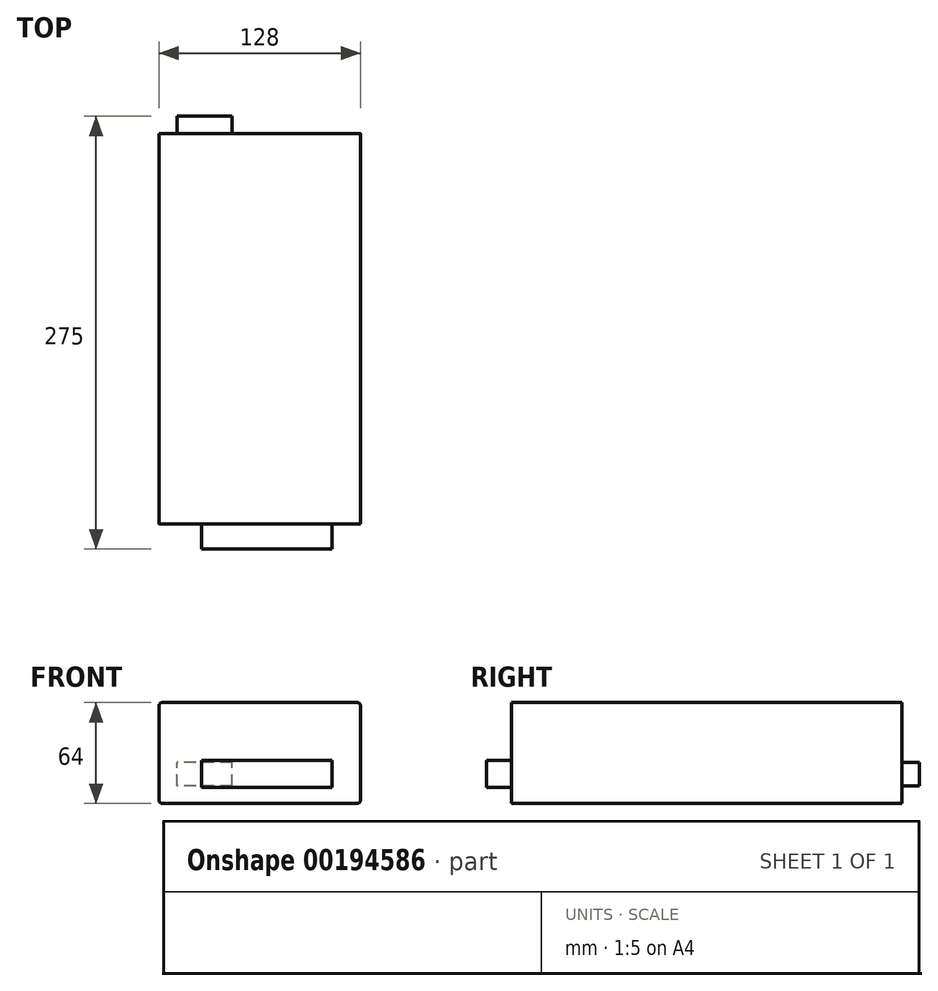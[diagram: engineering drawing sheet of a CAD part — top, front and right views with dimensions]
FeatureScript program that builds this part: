
annotation { "Feature Type Name" : "Feature", "Feature Type Description" : "" }
export const myFeature = defineFeature(function(context is Context, id is Id, definition is map)
    precondition{}
    {
        {
            var Q0;
            Q0=qCreatedBy(makeId("Front.planeOp"),FACE);
            var sketch = newSketch(context, id + "F0", { "sketchPlane" : qUnion([Q0])});
            skLineSegment(sketch, "E0.bottom", {"start": v(0, 0) * mm, "end": v(128, 0) * mm});
            skLineSegment(sketch, "E0.top", {"start": v(0, 64) * mm, "end": v(128, 64) * mm});
            skLineSegment(sketch, "E0.left", {"start": v(0, 0) * mm, "end": v(0, 64) * mm});
            skLineSegment(sketch, "E0.right", {"start": v(128, 0) * mm, "end": v(128, 64) * mm});
            skSolve(sketch);
        }
        {
            var Q0;
            Q0 = qSketchRegion(id + "F0", true);
            extrude(context, id + "F1", {"entities" : qUnion([Q0]), "depth" : 248 * mm});
        }
        {
            var Q0;
            Q0=makeQuery(id+"F1.opExtrude","CAP_FACE",FACE,{"disambiguationData":[OSD([sQuery(id+"F0.wireOp",EDGE,"E0.bottom"),sQuery(id+"F0.wireOp",EDGE,"E0.top"),sQuery(id+"F0.wireOp",EDGE,"E0.left"),sQuery(id+"F0.wireOp",EDGE,"E0.right")])],"isStart":false});
            var sketch = newSketch(context, id + "F2", { "sketchPlane" : qUnion([Q0])});
            skLineSegment(sketch, "E1", {"start": v(110, 10) * mm, "end": v(27, 10) * mm});
            skLineSegment(sketch, "E2", {"start": v(27, 10) * mm, "end": v(27, 27.33) * mm});
            skLineSegment(sketch, "E3", {"start": v(27, 27.33) * mm, "end": v(110, 27.33) * mm});
            skLineSegment(sketch, "E4", {"start": v(110, 27.33) * mm, "end": v(110, 10) * mm});
            skSolve(sketch);
        }
        {
            var Q0;
            Q0 = qSketchRegion(id + "F2", true);
            extrude(context, id + "F3", {"entities" : qUnion([Q0]), "operationType" : NewBodyOperationType.ADD, "depth" : 16 * mm});
        }
        {
            var Q0;
            Q0=makeQuery(id+"F1.opExtrude","CAP_FACE",FACE,{"disambiguationData":[OSD([sQuery(id+"F0.wireOp",EDGE,"E0.bottom"),sQuery(id+"F0.wireOp",EDGE,"E0.top"),sQuery(id+"F0.wireOp",EDGE,"E0.left"),sQuery(id+"F0.wireOp",EDGE,"E0.right")])],"isStart":true});
            var sketch = newSketch(context, id + "F4", { "sketchPlane" : qUnion([Q0])});
            skLineSegment(sketch, "E5.bottom", {"start": v(-46.5, 11) * mm, "end": v(-11.5, 11) * mm});
            skLineSegment(sketch, "E5.top", {"start": v(-46.5, 26) * mm, "end": v(-11.5, 26) * mm});
            skLineSegment(sketch, "E5.left", {"start": v(-46.5, 11) * mm, "end": v(-46.5, 26) * mm});
            skLineSegment(sketch, "E5.right", {"start": v(-11.5, 11) * mm, "end": v(-11.5, 26) * mm});
            skSolve(sketch);
        }
        {
            var Q0;
            Q0 = qSketchRegion(id + "F4", true);
            extrude(context, id + "F5", {"entities" : qUnion([Q0]), "operationType" : NewBodyOperationType.ADD, "depth" : 11 * mm});
        }
        {
            var Q0;
            Q0=makeQuery(id+"F1.opExtrude","SWEPT_EDGE",EDGE,{"disambiguationData":[OSD([sQuery(id+"F0.wireOp",EDGE,"E0.top"),sQuery(id+"F0.wireOp",EDGE,"E0.right")])]});
            var Q1;
            Q1=makeQuery(id+"F1.opExtrude","SWEPT_EDGE",EDGE,{"disambiguationData":[OSD([sQuery(id+"F0.wireOp",EDGE,"E0.bottom"),sQuery(id+"F0.wireOp",EDGE,"E0.right")])]});
            var Q2;
            Q2=makeQuery(id+"F1.opExtrude","SWEPT_EDGE",EDGE,{"disambiguationData":[OSD([sQuery(id+"F0.wireOp",EDGE,"E0.top"),sQuery(id+"F0.wireOp",EDGE,"E0.left")])]});
            var Q3;
            Q3=makeQuery(id+"F1.opExtrude","SWEPT_EDGE",EDGE,{"disambiguationData":[OSD([sQuery(id+"F0.wireOp",EDGE,"E0.bottom"),sQuery(id+"F0.wireOp",EDGE,"E0.left")])]});
            fillet(context, id + "F6", {"entities" : qUnion([Q0, Q1, Q2, Q3]), "radius" : 2 * mm, "tangentPropagation" : true, "allowEdgeOverflow" : false});
        }
    });
